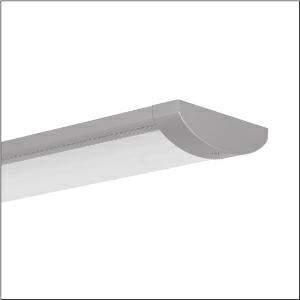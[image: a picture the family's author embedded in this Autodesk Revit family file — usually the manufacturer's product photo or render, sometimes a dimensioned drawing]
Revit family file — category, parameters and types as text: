
# Revit family: tv_20_5xa86174n0j
name_source: partatom
category: Lighting Fixtures
units: mm (PartAtom-declared; Revit-internal decimal feet)

## family parameters
Cut with Voids When Loaded = No
Host = Face
Light Source = No
Part Type = Normal
Room Calculation Point = No
Round Connector Dimension = Use Diameter
Shared = No

## types (1)
- TV 20 (1 x LED 4000K / CRI = 80 (unbekannt), 3960 lm, 4000K)
    Apparent Load = 37 VA
    CIE Flux Codes = 48 78 95 99 100
    Color Rendering = 80
    Color Temperature = 4000K
    Default Elevation = 1800 mm
    Description = TV 20, vandal-proof luminaire, primary light control with specular reflector, of aluminium, matt, primary optical cover: enclosure, of PC, frosted, light emission: direct distribution, primary light characteristic: symmetric, installation type: surface-mounted, LED, rated luminous flux: 3.960lm, luminous efficacy: 107lm/W, light colour: 840, colour temperature: 4000K, control gear: ON/OFF, mains connection: 230V, AC, 50Hz, rated input power: 37W, luminaire housing, of aluminium, coated, SITECO metallic grey (DB 702S), with wall and ceiling fixing element, length: 1.261mm, width: 260mm, height: 70mm, mounting height: 2.5..4.0m, protection rating (complete): IP65, insulation class (complete): insulation class I (protective earthing), certification: CE, protection symbol: F, impact resistance: 2x IK10, standard: EN 60598, packaging unit: 1 piece
    Height = 70 mm
    Lamp = 1 x LED 4000K / CRI >= 80 (unbekannt)
    Lamp Light Flux = 3960 lm
    Lamp count = 1
    Length = 1261 mm
    Luminous efficacy = 107 lm/W
    Manufacturer = Siteco
    ModVariant = No
    Model = 5XA86174N0J
    Mounting Place = Ceiling
    Mounting Type = Surface mounted
    Number of Poles = 1
    OnlyDefault = Yes
    Power Factor = 1
    Product Name = TV 20
    Product group = vandal-proof luminaire
    ProductGroupID = 310
    Protection Class = Protection class I
    Protection Degree = IP 65
    RLX_Detail_Level = 1
    RLX_Emergency_Light_Flux = 0 lm
    RLX_Emergency_Type = 0
    RLX_Emergency_Type_DB = No
    RlxData = <blob elided: 25529 chars, md5=0dccf7bd>
    Socket = socket
    Standby Power = 0 W
    System Light Flux = 3960 lm
    System Power = 37 W
    Type Comments = Product without accessories
    Type Image = l_1004809.jpg
    URL = http://relux.com
    VarID = ---
    Voltage = 0 V
    Weight = 0.00 kg
    Width = 260 mm

## geometry (parser evidence)
native form markers: Blend x4, Sweep x12
no freeform markers — native parametric forms only
